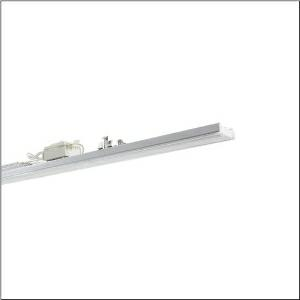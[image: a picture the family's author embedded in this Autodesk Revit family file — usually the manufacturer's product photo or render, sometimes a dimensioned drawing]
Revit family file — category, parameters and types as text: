
# Revit family: licross_r__11_recessed_mo_51te12dv4fxg_eeda
name_source: partatom
category: Lighting Fixtures
units: mm (PartAtom-declared; Revit-internal decimal feet)

## family parameters
Cut with Voids When Loaded = No
Host = Face
Light Source = No
Part Type = Normal
Room Calculation Point = No
Round Connector Dimension = Use Diameter
Shared = No

## types (1)
- --- (1 x LED, 15360 lm, 84.1 W, 4000K)
    Apparent Load = 84 VA
    CIE Flux Codes = 67 92 99 100 100
    Color Rendering = 80
    Color Temperature = 4000K
    Default Elevation = 1800 mm
    Description = Licross® 11 Recessed MO, luminaire insert, of sheet steel, galvanised, coil coated, white, length: 2.250mm, width: 66mm, height: 67mm, LED rated luminous flux: 15.360lm, light colour: 840, control gear: DALI 2, with plug, 5-pole, with phase selection, mains connection: 220..240V, AC, 50/60Hz, rated input power: 84W, internal wiring halogen-free, primary optical cover: cover, of PMMA, light emission: direct distribution, primary light characteristic: symmetric, protection rating (complete): IP54, insulation class (complete): insulation class I (protective earthing), certification: CE, ENEC, VDE, UKCA, protection symbol: D if used in an environment with non-conductive dust loads with corresponding accessories, impact resistance: IK06, permissible ambient temperature for indoor applications: -25..+35°C, corresponds to IFS (International Featured Standards) requirements for safety and quality in the food industry, reducing of maximum allowable ambient temperature of 5°C with ceiling mounting, LABS conformity tested according to VDMA 24364:2018-05, packaging unit: 1 piece
    Height = 58 mm
    Lamp = 1 x LED
    Lamp Light Flux = 15360 lm
    Lamp Power = 84.1 W
    Lamp count = 1
    Length = 2250 mm
    Luminous efficacy = 183 lm/W
    Manufacturer = Siteco
    ModVariant = No
    Model = 51TE12DV4FXG
    Mounting Place = Ceiling
    Mounting Type = Pendant
    Number of Poles = 1
    OnlyDefault = Yes
    Power Factor = 1
    Product Name = Licross® 11 Recessed MO
    Product group = luminaire insert | ceiling pendant
    ProductGroupID = 902
    Protection Class = Protection class I
    Protection Degree = IP 54
    RLX_Detail_Level = 1
    RLX_Emergency_Light_Flux = 0 lm
    RLX_Emergency_Type = 0
    RLX_Emergency_Type_DB = No
    RlxData = <blob elided: 29237 chars, md5=b73df762>
    Socket = socket
    Standby Power = 0 W
    System Light Flux = 15360 lm
    System Power = 84 W
    Type Comments = factory setting: luminous flux: 100 % | dim-lin: 254 | 378 mA
    Type Image = l_1296930.jpg
    URL = http://relux.com
    VarID = @adj_121579
    Voltage = 0 V
    Weight = 0.00 kg
    Width = 66 mm

## geometry (parser evidence)
native form markers: Blend x4, Sweep x9
no freeform markers — native parametric forms only
